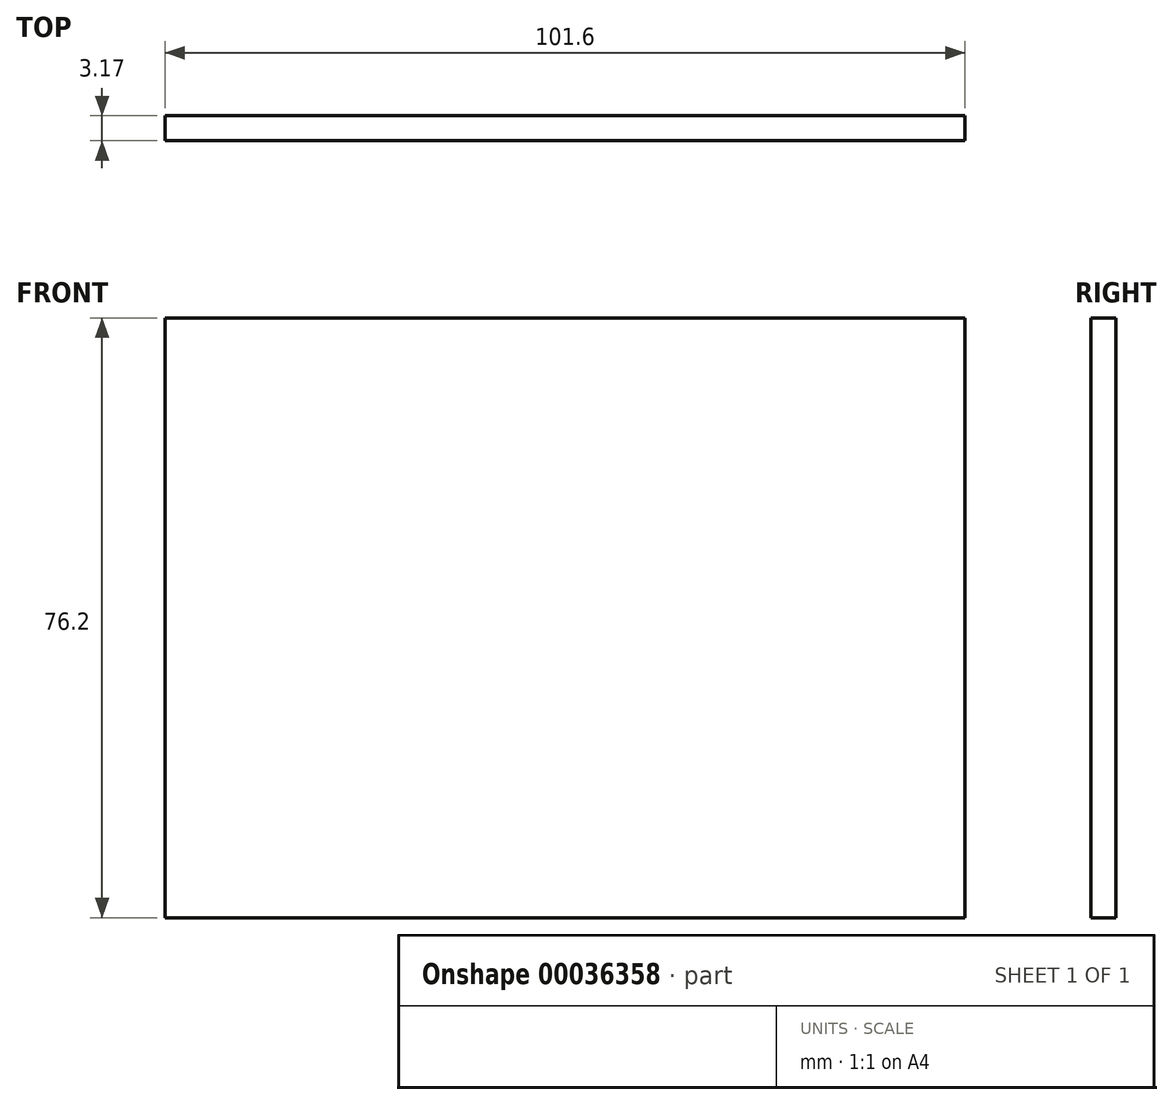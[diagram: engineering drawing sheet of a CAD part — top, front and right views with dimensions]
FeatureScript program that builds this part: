
annotation { "Feature Type Name" : "Feature", "Feature Type Description" : "" }
export const myFeature = defineFeature(function(context is Context, id is Id, definition is map)
    precondition{}
    {
        {
            var Q0;
            Q0=qCreatedBy(makeId("Front.planeOp"),FACE);
            var sketch = newSketch(context, id + "F0", { "sketchPlane" : qUnion([Q0])});
            skLineSegment(sketch, "E0.rect.bottom", {"start": v(-50.8, 38.1) * mm, "end": v(50.8, 38.1) * mm});
            skLineSegment(sketch, "E0.rect.top", {"start": v(-50.8, -38.1) * mm, "end": v(50.8, -38.1) * mm});
            skLineSegment(sketch, "E0.rect.left", {"start": v(-50.8, 38.1) * mm, "end": v(-50.8, -38.1) * mm});
            skLineSegment(sketch, "E0.rect.right", {"start": v(50.8, 38.1) * mm, "end": v(50.8, -38.1) * mm});
            skPoint(sketch, "E0.rect.middle", {"position": v(0, 0) * mm});
            skSolve(sketch);
        }
        {
            var Q0;
            Q0=makeQuery(id+"F0.imprint","IMPRINT",FACE,{"disambiguationData":[TD([[makeQuery(id+"F0.imprint","IMPRINT",EDGE,{"derivedFrom":sQuery(id+"F0.wireOp",EDGE,"E0.rect.bottom")}),-1.0]])]});
            extrude(context, id + "F1", {"entities" : qUnion([Q0]), "depth" : 3.17 * mm});
        }
    });
